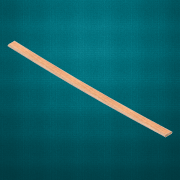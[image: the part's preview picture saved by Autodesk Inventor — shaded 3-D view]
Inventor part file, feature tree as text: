
AUTODESK INVENTOR PART (.ipt)
format: ipt  version: 2017 (Build 210142000, 142)  size: 154,624 bytes
history: native  units: in
note: dims shown in document units (in); Inventor stores cm internally (conversion verified against a paired STEP export)
features: sketch x2, extrude x1, fillet x1, other x1
ambient origin geometry x8: Origin, YZ Plane, XZ Plane, XY Plane, X Axis, Y Axis, Z Axis, Center Point
bodies: Solid1 (feature_tree)
feature tree (5):
  extrude  "Extrusion1"  Depth=1.375in
  fillet  "Fillet1"  Radius=30.0in
  other  "Bend Part1"
  sketch  "Sketch1"  dims[d0=1.375in d1=0.375in d2=30.0in d3=0.0in]
  sketch  "Sketch2"  dims[d4=0.125in d5=346.0in d6=0.0344in]
